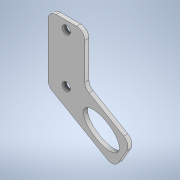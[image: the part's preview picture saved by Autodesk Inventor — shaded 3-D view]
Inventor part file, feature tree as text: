
AUTODESK INVENTOR PART (.ipt)
format: ipt  version: 2022 (Build 260153000, 153)  size: 144,896 bytes
history: native  units: mm
features: extrude x2
ambient origin geometry x8: Origin, YZ Plane, XZ Plane, XY Plane, X Axis, Y Axis, Z Axis, Center Point
bodies: Solid1 (feature_tree)
feature tree (2):
  extrude  "Extrusion1"  Depth=10.0mm
  extrude  "Extrusion2"  Depth=40.0mm
